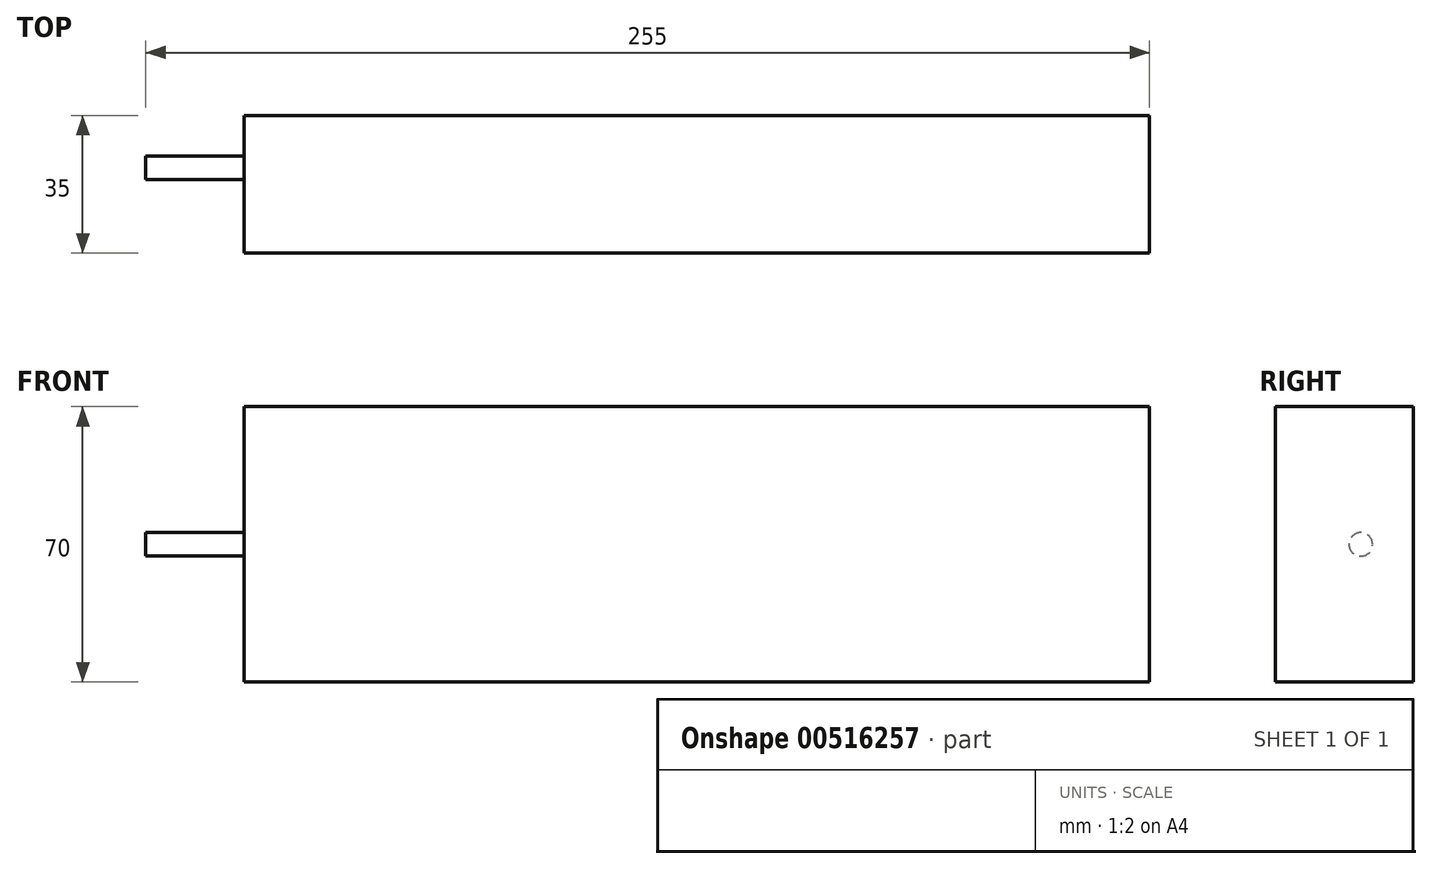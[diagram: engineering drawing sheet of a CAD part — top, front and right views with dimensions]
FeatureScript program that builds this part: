
annotation { "Feature Type Name" : "Feature", "Feature Type Description" : "" }
export const myFeature = defineFeature(function(context is Context, id is Id, definition is map)
    precondition{}
    {
        {
            var Q0;
            Q0=qCreatedBy(makeId("Front.planeOp"),FACE);
            var sketch = newSketch(context, id + "F0", { "sketchPlane" : qUnion([Q0])});
            skLineSegment(sketch, "E0.bottom", {"start": v(115, -35) * mm, "end": v(-115, -35) * mm});
            skLineSegment(sketch, "E0.top", {"start": v(115, 35) * mm, "end": v(-115, 35) * mm});
            skLineSegment(sketch, "E0.left", {"start": v(115, -35) * mm, "end": v(115, 35) * mm});
            skLineSegment(sketch, "E0.right", {"start": v(-115, -35) * mm, "end": v(-115, 35) * mm});
            skPoint(sketch, "E0.middle", {"position": v(0, 0) * mm});
            skSolve(sketch);
        }
        {
            var Q0;
            Q0 = qSketchRegion(id + "F0", true);
            extrude(context, id + "F1", {"entities" : qUnion([Q0]), "depth" : 35 * mm, "offsetDistance" : 25 * mm});
        }
        {
            var Q0;
            Q0=makeQuery(id+"F1.opExtrude","SWEPT_FACE",FACE,{"disambiguationData":[OSD([sQuery(id+"F0.wireOp",EDGE,"E0.right")])]});
            var sketch = newSketch(context, id + "F2", { "sketchPlane" : qUnion([Q0])});
            skCircle(sketch, "E1", {"center": v(13.34, 0) * mm, "radius": 3 * mm});
            skPoint(sketch, "E1.centerSnap0", {"position": v(35, 0) * mm});
            skSolve(sketch);
        }
        {
            var Q0;
            Q0 = qSketchRegion(id + "F2", true);
            extrude(context, id + "F3", {"entities" : qUnion([Q0]), "operationType" : NewBodyOperationType.ADD, "depth" : 25 * mm, "offsetDistance" : 25 * mm});
        }
    });
